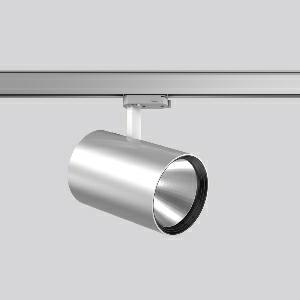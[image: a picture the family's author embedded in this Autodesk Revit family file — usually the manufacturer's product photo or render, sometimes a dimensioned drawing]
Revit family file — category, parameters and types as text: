
# Revit family: deecos_s_maxi_742241_004_2_3e56
name_source: partatom
category: Lighting Fixtures
units: mm (PartAtom-declared; Revit-internal decimal feet)

## family parameters
Cut with Voids When Loaded = No
Host = Face
Light Source = No
Part Type = Normal
Room Calculation Point = No
Round Connector Dimension = Use Diameter
Shared = No

## types (1)
- DEECOS S maxi (1 x LED Modul 927 bakery, 3300 lm, 2700)
    Apparent Load = 33 VA
    Approval mark = CE
    CIE Flux Codes = 100 100 100 100 100
    Color Rendering = 90
    Color Temperature = 2700
    Default Elevation = 1800 mm
    Description = Series: DEECOS S maxi
LED surface-mounted projector in modern design with no visible cooling ribs. Housing: die-cast aluminium, powder-coated. Rotation range: 356°. Swivel range: 90°. Black plastic ring and recessed LED to prevent glare from the side. Optical assembly with reflector made of MIRO-Silver with 98% total light reflection for outstanding efficiency - can be changed without tools. Special LED for illumination of pastries included. With multi adaptor for 3-circuit tracks 230 V. Suitable for Track on ceiling, Wall track. High quality converter without flickering and stroboscopic effect. The following accessories can be mounted without use of tools: interchangeable lenses, decorative glasses, honeycomb louvre, clear and frosted diffusers, white interchangeable plastic ring. 
Colour: silver
Diameter: 123 mm
Height: 200 mm
Lamp: LED
Socket: without socket
Colour temperature: bakery
System power: 33 W
Rated luminous flux: 3300 lm
Luminous efficiency: 100 lm/W
Control gear: Regulated power supply
Protection class: I
Type of protection: IP 20
    Height = 200 mm  [stored 0.656168 ft]
    Lamp = 1 x LED Modul 927 bakery
    Lamp Light Flux = 3300 lm
    Lamp count = 1
    Length = 123 mm
    Lifetime = 50000 h
    Luminous efficacy = 100 lm/W
    Manufacturer = RZB
    ModVariant = No
    Model = 742241.004.2
    Mounting Place = Ceiling
    Mounting Type = Rail mounted
    Number of Poles = 1
    OnlyDefault = Yes
    Power Factor = 1
    Product Name = DEECOS S maxi
    Product group = Track mounted projectors
    ProductGroupID = 301
    Protection Class = Protection class I
    Protection Degree = IP 20
    RLX_Detail_Level = 1
    RLX_Emergency_Light_Flux = 0 lm
    RLX_Emergency_Type = 0
    RLX_Emergency_Type_DB = No
    RlxData = <blob elided: 40549 chars, md5=ce290d15>
    Socket = socket
    Standby Power = 0 W
    System Light Flux = 3300 lm
    System Power = 33 W
    Type Comments = Product without accessories
    Type Image = 741954.004.jpg
    URL = http://relux.com
    VarID = ---
    Voltage = 230 V
    Voltage Range = 220-240 V
    Weight = 0.00 kg
    Width = 0 mm  [stored 0 ft]

note: [stored X ft] marks values corroborated as IEEE doubles in the binary element streams (Revit-internal decimal feet)

## geometry (parser evidence)
native form markers: Blend x4, Sweep x12
no freeform markers — native parametric forms only
